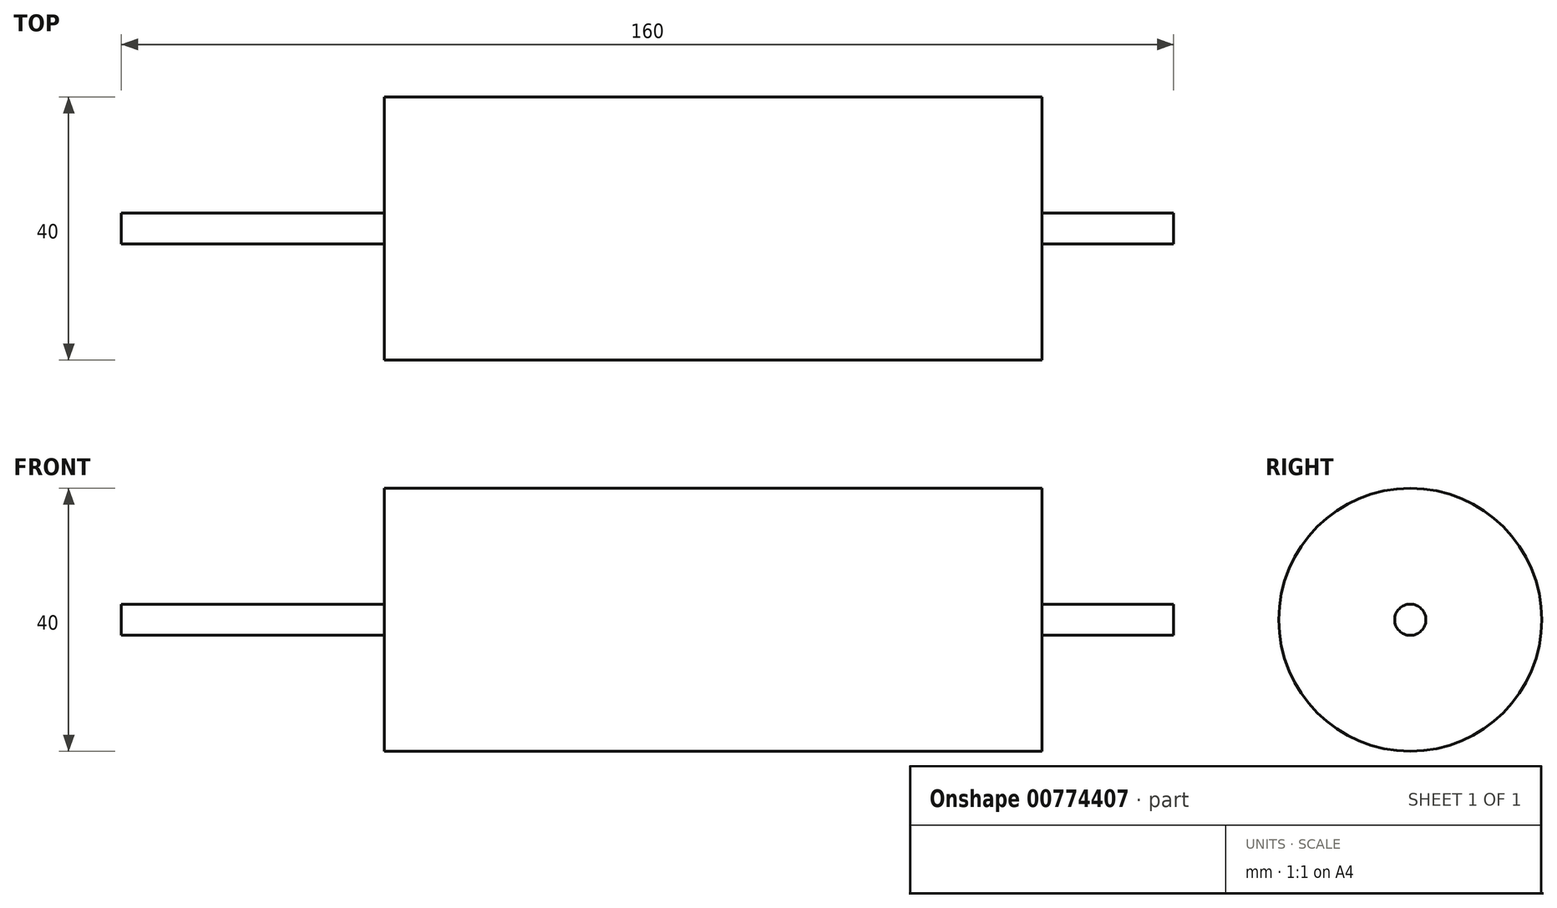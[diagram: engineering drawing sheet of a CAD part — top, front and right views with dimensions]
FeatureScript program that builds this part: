
annotation { "Feature Type Name" : "Feature", "Feature Type Description" : "" }
export const myFeature = defineFeature(function(context is Context, id is Id, definition is map)
    precondition{}
    {
        {
            var Q0;
            Q0=qCreatedBy(makeId("Right.planeOp"),FACE);
            var sketch = newSketch(context, id + "F0", { "sketchPlane" : qUnion([Q0])});
            skCircle(sketch, "E0", {"center": v(0, 0) * mm, "radius": 20 * mm});
            skSolve(sketch);
        }
        {
            var Q0;
            Q0 = qSketchRegion(id + "F0", true);
            extrude(context, id + "F1", {"entities" : qUnion([Q0]), "depth" : 100 * mm, "offsetDistance" : 25 * mm});
        }
        {
            var Q0;
            Q0=makeQuery(id+"F1.opExtrude","CAP_FACE",FACE,{"disambiguationData":[OSD([sQuery(id+"F0.wireOp",EDGE,"E0")])],"isStart":false});
            var sketch = newSketch(context, id + "F2", { "sketchPlane" : qUnion([Q0])});
            skCircle(sketch, "E1", {"center": v(0, 0) * mm, "radius": 2.38 * mm});
            skSolve(sketch);
        }
        {
            var Q0;
            Q0 = qSketchRegion(id + "F2", true);
            extrude(context, id + "F3", {"entities" : qUnion([Q0]), "operationType" : NewBodyOperationType.ADD, "depth" : 20 * mm, "offsetDistance" : 25 * mm});
        }
        {
            var Q0;
            Q0=makeQuery(id+"F0.imprint","IMPRINT",FACE,{"disambiguationData":[TD([[makeQuery(id+"F0.imprint","IMPRINT",EDGE,{"derivedFrom":sQuery(id+"F0.wireOp",EDGE,"E0")}),1.0]])]});
            var sketch = newSketch(context, id + "F4", { "sketchPlane" : qUnion([Q0])});
            skCircle(sketch, "E2", {"center": v(0, 0) * mm, "radius": 2.37 * mm});
            skSolve(sketch);
        }
        {
            var Q0;
            Q0 = qSketchRegion(id + "F4", true);
            extrude(context, id + "F5", {"entities" : qUnion([Q0]), "operationType" : NewBodyOperationType.ADD, "oppositeDirection" : true, "depth" : 40 * mm, "offsetDistance" : 25 * mm});
        }
    });
